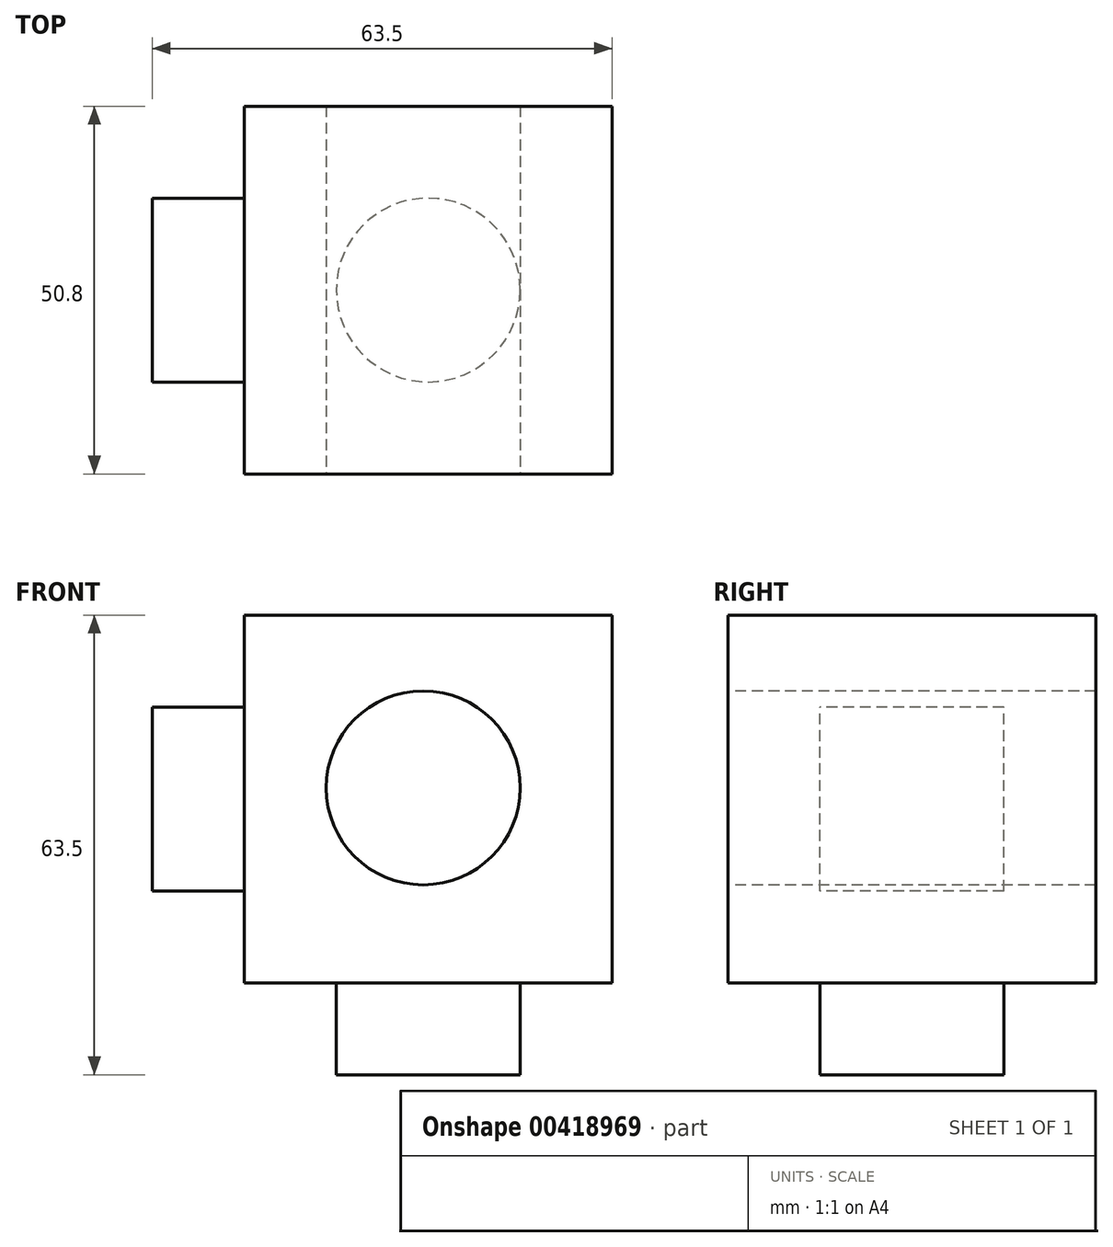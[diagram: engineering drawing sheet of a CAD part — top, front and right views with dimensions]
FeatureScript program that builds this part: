
annotation { "Feature Type Name" : "Feature", "Feature Type Description" : "" }
export const myFeature = defineFeature(function(context is Context, id is Id, definition is map)
    precondition{}
    {
        {
            var Q0;
            Q0=qCreatedBy(makeId("Front.planeOp"),FACE);
            var sketch = newSketch(context, id + "F0", { "sketchPlane" : qUnion([Q0])});
            skLineSegment(sketch, "E0.bottom", {"start": v(0, 0) * mm, "end": v(-50.8, 0) * mm});
            skLineSegment(sketch, "E0.top", {"start": v(0, 50.8) * mm, "end": v(-50.8, 50.8) * mm});
            skLineSegment(sketch, "E0.left", {"start": v(0, 0) * mm, "end": v(0, 50.8) * mm});
            skLineSegment(sketch, "E0.right", {"start": v(-50.8, 0) * mm, "end": v(-50.8, 50.8) * mm});
            skSolve(sketch);
        }
        {
            var Q0;
            Q0 = qSketchRegion(id + "F0", true);
            extrude(context, id + "F1", {"entities" : qUnion([Q0]), "depth" : 50.8 * mm});
        }
        {
            var Q0;
            Q0=makeQuery(id+"F1.opExtrude","CAP_FACE",FACE,{"disambiguationData":[OSD([sQuery(id+"F0.wireOp",EDGE,"E0.bottom"),sQuery(id+"F0.wireOp",EDGE,"E0.top"),sQuery(id+"F0.wireOp",EDGE,"E0.left"),sQuery(id+"F0.wireOp",EDGE,"E0.right")])],"isStart":false});
            var sketch = newSketch(context, id + "F2", { "sketchPlane" : qUnion([Q0])});
            skCircle(sketch, "E1", {"center": v(-26.1, 26.92) * mm, "radius": 13.4 * mm});
            skSolve(sketch);
        }
        {
            var Q0;
            Q0 = qSketchRegion(id + "F2", true);
            extrude(context, id + "F3", {"entities" : qUnion([Q0]), "operationType" : NewBodyOperationType.REMOVE, "oppositeDirection" : true, "depth" : 61.72 * mm});
        }
        {
            var Q0;
            Q0=makeQuery(id+"F1.opExtrude","SWEPT_FACE",FACE,{"disambiguationData":[OSD([sQuery(id+"F0.wireOp",EDGE,"E0.right")])]});
            var sketch = newSketch(context, id + "F4", { "sketchPlane" : qUnion([Q0])});
            skLineSegment(sketch, "E2.bottom", {"start": v(12.7, 12.7) * mm, "end": v(38.1, 12.7) * mm});
            skLineSegment(sketch, "E2.top", {"start": v(12.7, 38.1) * mm, "end": v(38.1, 38.1) * mm});
            skLineSegment(sketch, "E2.left", {"start": v(12.7, 12.7) * mm, "end": v(12.7, 38.1) * mm});
            skLineSegment(sketch, "E2.right", {"start": v(38.1, 12.7) * mm, "end": v(38.1, 38.1) * mm});
            skSolve(sketch);
        }
        {
            var Q0;
            Q0=makeQuery(id+"F4.imprint","IMPRINT",FACE,{"disambiguationData":[TD([[makeQuery(id+"F4.imprint","IMPRINT",EDGE,{"derivedFrom":sQuery(id+"F4.wireOp",EDGE,"E2.bottom")}),1.0]])]});
            extrude(context, id + "F5", {"entities" : qUnion([Q0]), "operationType" : NewBodyOperationType.ADD, "depth" : 12.7 * mm});
        }
        {
            var Q0;
            Q0=makeQuery(id+"F1.opExtrude","SWEPT_FACE",FACE,{"disambiguationData":[OSD([sQuery(id+"F0.wireOp",EDGE,"E0.bottom")])]});
            var sketch = newSketch(context, id + "F6", { "sketchPlane" : qUnion([Q0])});
            skCircle(sketch, "E3", {"center": v(-25.4, 25.4) * mm, "radius": 12.7 * mm});
            skSolve(sketch);
        }
        {
            var Q0;
            Q0=makeQuery(id+"F6.imprint","IMPRINT",FACE,{"disambiguationData":[TD([[makeQuery(id+"F6.imprint","IMPRINT",EDGE,{"derivedFrom":sQuery(id+"F6.wireOp",EDGE,"E3")}),1.0]])]});
            extrude(context, id + "F7", {"entities" : qUnion([Q0]), "operationType" : NewBodyOperationType.ADD, "depth" : 12.7 * mm});
        }
    });
